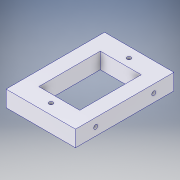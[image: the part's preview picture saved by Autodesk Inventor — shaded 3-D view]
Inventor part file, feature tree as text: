
AUTODESK INVENTOR PART (.ipt)
format: ipt  version: 2017 (Build 210142000, 142)  size: 137,728 bytes
history: native  units: in
note: dims shown in document units (in); Inventor stores cm internally (conversion verified against a paired STEP export)
features: extrude x5, sketch x5, projected_geometry x2
ambient origin geometry x8: Origin, YZ Plane, XZ Plane, XY Plane, X Axis, Y Axis, Z Axis, Center Point
bodies: Solid1 (feature_tree)
feature tree (12):
  extrude  "Extrusion1"  Depth=1.6929in
  extrude  "Extrusion2"  Depth=0.3937in
  extrude  "Extrusion3"  Depth=0.1969in TaperAngle=0.0deg
  extrude  "Extrusion4"  Depth=0.1969in
  extrude  "Extrusion5"  Depth=0.3937in
  sketch  "Sketch1"  dims[d0=2.4016in d1=1.6929in]
  sketch  "Sketch2"  dims[d2=0.3937in d3=0.0in d4=0.4921in]
  sketch  "Sketch3"  dims[d5=0.0984in d6=0.1969in d7=0.0in]
  projected_geometry  "Projected Loop1"
  sketch  "Sketch4"  dims[d8=0.1969in d9=0.0in d10=0.25in]
  sketch  "Sketch5"  dims[d11=0.25in d12=0.0984in d13=0.0984in d14=0.3937in d15=0.0in d16=1.0in d17=1.5in d18=0.3937in d19=0.0in]
  projected_geometry  "Projected Loop2"
